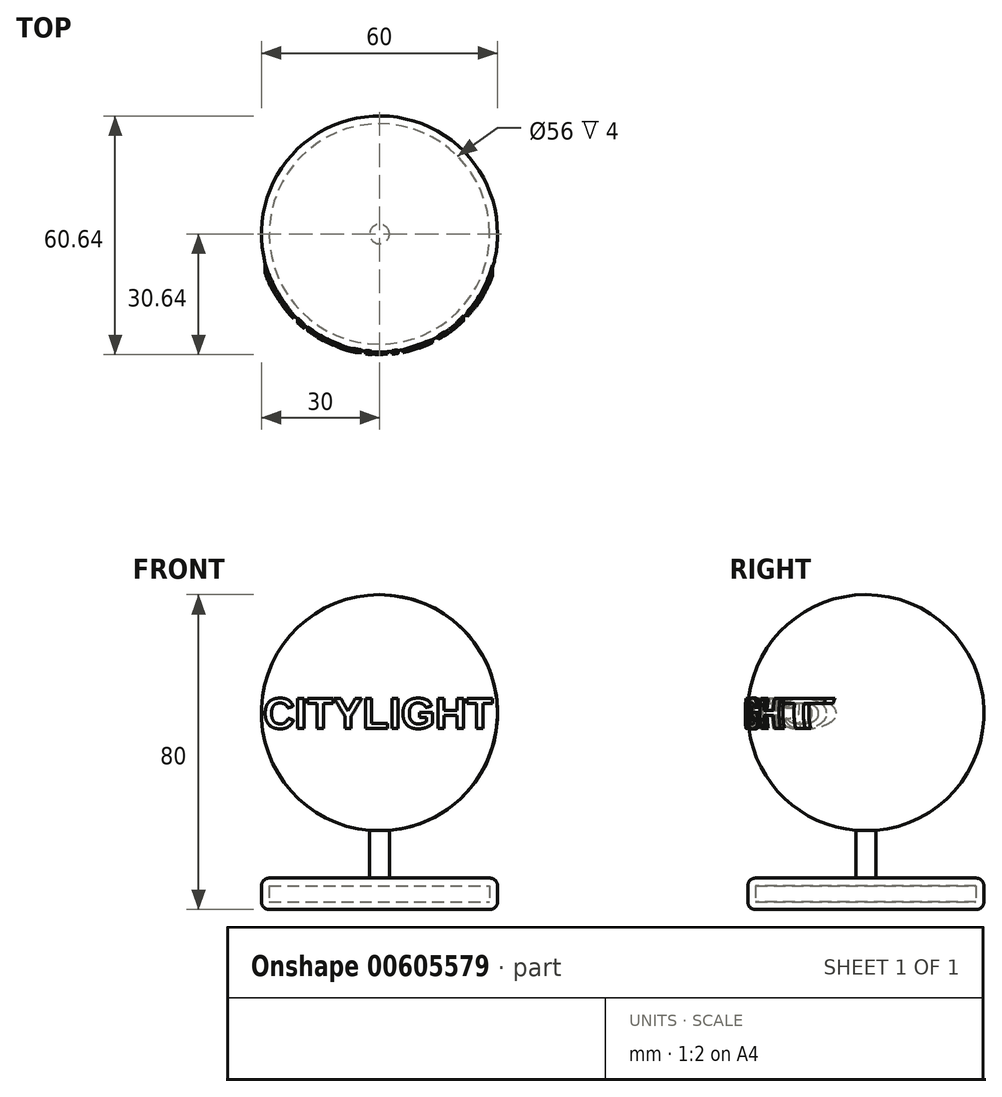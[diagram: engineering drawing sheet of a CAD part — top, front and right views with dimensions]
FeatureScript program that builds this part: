
annotation { "Feature Type Name" : "Feature", "Feature Type Description" : "" }
export const myFeature = defineFeature(function(context is Context, id is Id, definition is map)
    precondition{}
    {
        {
            var Q0;
            Q0=qCreatedBy(makeId("Top.planeOp"),FACE);
            var sketch = newSketch(context, id + "F0", { "sketchPlane" : qUnion([Q0])});
            skCircle(sketch, "E0", {"center": v(0, 0) * mm, "radius": 30 * mm});
            skSolve(sketch);
        }
        {
            var Q0;
            Q0=makeQuery(id+"F0.imprint","IMPRINT",FACE,{"disambiguationData":[TD([[makeQuery(id+"F0.imprint","IMPRINT",EDGE,{"derivedFrom":sQuery(id+"F0.wireOp",EDGE,"E0")}),1.0]])]});
            extrude(context, id + "F1", {"entities" : qUnion([Q0]), "depth" : 8 * mm, "offsetDistance" : 25 * mm});
        }
        {
            var Q0;
            Q0=makeQuery(id+"F1.opExtrude","CAP_EDGE",EDGE,{"disambiguationData":[OSD([sQuery(id+"F0.wireOp",EDGE,"E0")])],"isStart":false});
            var Q1;
            Q1=makeQuery(id+"F1.opExtrude","CAP_EDGE",EDGE,{"disambiguationData":[OSD([sQuery(id+"F0.wireOp",EDGE,"E0")])],"isStart":true});
            fillet(context, id + "F2", {"entities" : qUnion([Q0, Q1]), "radius" : 2 * mm, "tangentPropagation" : true, "allowEdgeOverflow" : false});
        }
        {
            var Q0;
            Q0=qCreatedBy(makeId("Front.planeOp"),FACE);
            var sketch = newSketch(context, id + "F3", { "sketchPlane" : qUnion([Q0])});
            skLineSegment(sketch, "E1", {"start": v(0, 80) * mm, "end": v(0, 78) * mm});
            skArc(sketch, "E2", {"start": v(2.5, 20.1) * mm, "mid": v(29.97, 51.25) * mm, "end": v(0, 80) * mm});
            skLineSegment(sketch, "E3", {"start": v(0, 20) * mm, "end": v(0, 8) * mm});
            skLineSegment(sketch, "E4", {"start": v(0, 8) * mm, "end": v(2.5, 8) * mm});
            skLineSegment(sketch, "E5", {"start": v(2.5, 8) * mm, "end": v(2.5, 20.1) * mm});
            skArc(sketch, "E6.0", {"start": v(0, 22) * mm, "mid": v(28, 50) * mm, "end": v(0, 78) * mm});
            skLineSegment(sketch, "E7.trimOffspring", {"start": v(0, 22) * mm, "end": v(0, 20) * mm});
            skLineSegment(sketch, "E8", {"start": v(0, 0) * mm, "end": v(0, 88) * mm});
            skSolve(sketch);
        }
        {
            var Q0;
            Q0=qCreatedBy(makeId("Front.planeOp"),FACE);
            var sketch = newSketch(context, id + "F4", { "sketchPlane" : qUnion([Q0])});
            skLineSegment(sketch, "E9.0", {"start": v(-28, 8) * mm, "end": v(28, 8) * mm, "construction": true});
            skArc(sketch, "E10", {"start": v(30, 6) * mm, "mid": v(29.41, 7.41) * mm, "end": v(28, 8) * mm, "construction": true});
            skLineSegment(sketch, "E11", {"start": v(30, 6) * mm, "end": v(30, 2) * mm, "construction": true});
            skArc(sketch, "E12", {"start": v(28, 0) * mm, "mid": v(29.41, 0.59) * mm, "end": v(30, 2) * mm, "construction": true});
            skLineSegment(sketch, "E13", {"start": v(0, 0) * mm, "end": v(28, 0) * mm, "construction": true});
            skLineSegment(sketch, "E14.0", {"start": v(0, 6) * mm, "end": v(28, 6) * mm});
            skLineSegment(sketch, "E15.0", {"start": v(28, 6) * mm, "end": v(28, 6) * mm});
            skLineSegment(sketch, "E16.0", {"start": v(28, 6) * mm, "end": v(28, 2) * mm});
            skLineSegment(sketch, "E17.0", {"start": v(28, 2) * mm, "end": v(28, 2) * mm});
            skLineSegment(sketch, "E18.0", {"start": v(0, 2) * mm, "end": v(28, 2) * mm});
            skLineSegment(sketch, "E19", {"start": v(0, 6) * mm, "end": v(0, 2) * mm});
            skSolve(sketch);
        }
        {
            var Q0;
            Q0 = qSketchRegion(id + "F4", true);
            var Q1;
            Q1=sQuery(id+"F3.wireOp",EDGE,"E3");
            revolve(context, id + "F5", {"operationType" : NewBodyOperationType.REMOVE, "entities" : qUnion([Q0]), "axis" : qUnion([Q1]), "revolveType" : RevolveType.FULL, "oppositeDirection" : true});
        }
        {
            var Q0;
            Q0 = qSketchRegion(id + "F3", true);
            var Q1;
            Q1=sQuery(id+"F3.wireOp",EDGE,"E1");
            revolve(context, id + "F6", {"entities" : qUnion([Q0]), "axis" : qUnion([Q1]), "revolveType" : RevolveType.FULL});
        }
        {
            var Q0;
            Q0=qCreatedBy(makeId("Front.planeOp"),FACE);
            var sketch = newSketch(context, id + "F7", { "sketchPlane" : qUnion([Q0])});
            skArc(sketch, "E20.0", {"start": v(1.02, 19.32) * mm, "mid": v(30.7, 50.51) * mm, "end": v(0, 80.7) * mm});
            skSolve(sketch);
        }
        {
            var Q0;
            Q0 = qSketchRegion(id + "F7", true);
            var Q1;
            Q1=sQuery(id+"F7.wireOp",EDGE,"E20.0");
            var Q2;
            Q2=sQuery(id+"F3.wireOp",EDGE,"E1");
            revolve(context, id + "F8", {"bodyType" : ToolBodyType.SURFACE, "entities" : qUnion([Q0]), "surfaceEntities" : qUnion([Q1]), "axis" : qUnion([Q2]), "revolveType" : RevolveType.FULL});
        }
        {
            var Q0;
            Q0=qCreatedBy(makeId("Front.planeOp"),FACE);
            var sketch = newSketch(context, id + "F9", { "sketchPlane" : qUnion([Q0])});
            skText(sketch, "E21", { "text": "CITYLIGHT", "fontName": "Arimo-Bold.ttf"});
            const initialGuessF9  = {"E21": [-0.0295, 0.04602, 1, 0, 0.00796]};
            skSetInitialGuess(sketch, initialGuessF9);
            skSolve(sketch);
        }
        {
            var Q0;
            Q0 = qSketchRegion(id + "F9", true);
            var Q1;
            Q1=makeQuery(id+"F8.opRevolve","SWEPT_FACE",FACE,{"disambiguationData":[OSD([sQuery(id+"F7.wireOp",EDGE,"E20.0")])]});
            extrude(context, id + "F10", {"entities" : qUnion([Q0]), "operationType" : NewBodyOperationType.ADD, "endBound" : BoundingType.UP_TO_SURFACE, "depth" : 25 * mm, "endBoundEntityFace" : qUnion([Q1]), "offsetDistance" : 25 * mm});
        }
    });
